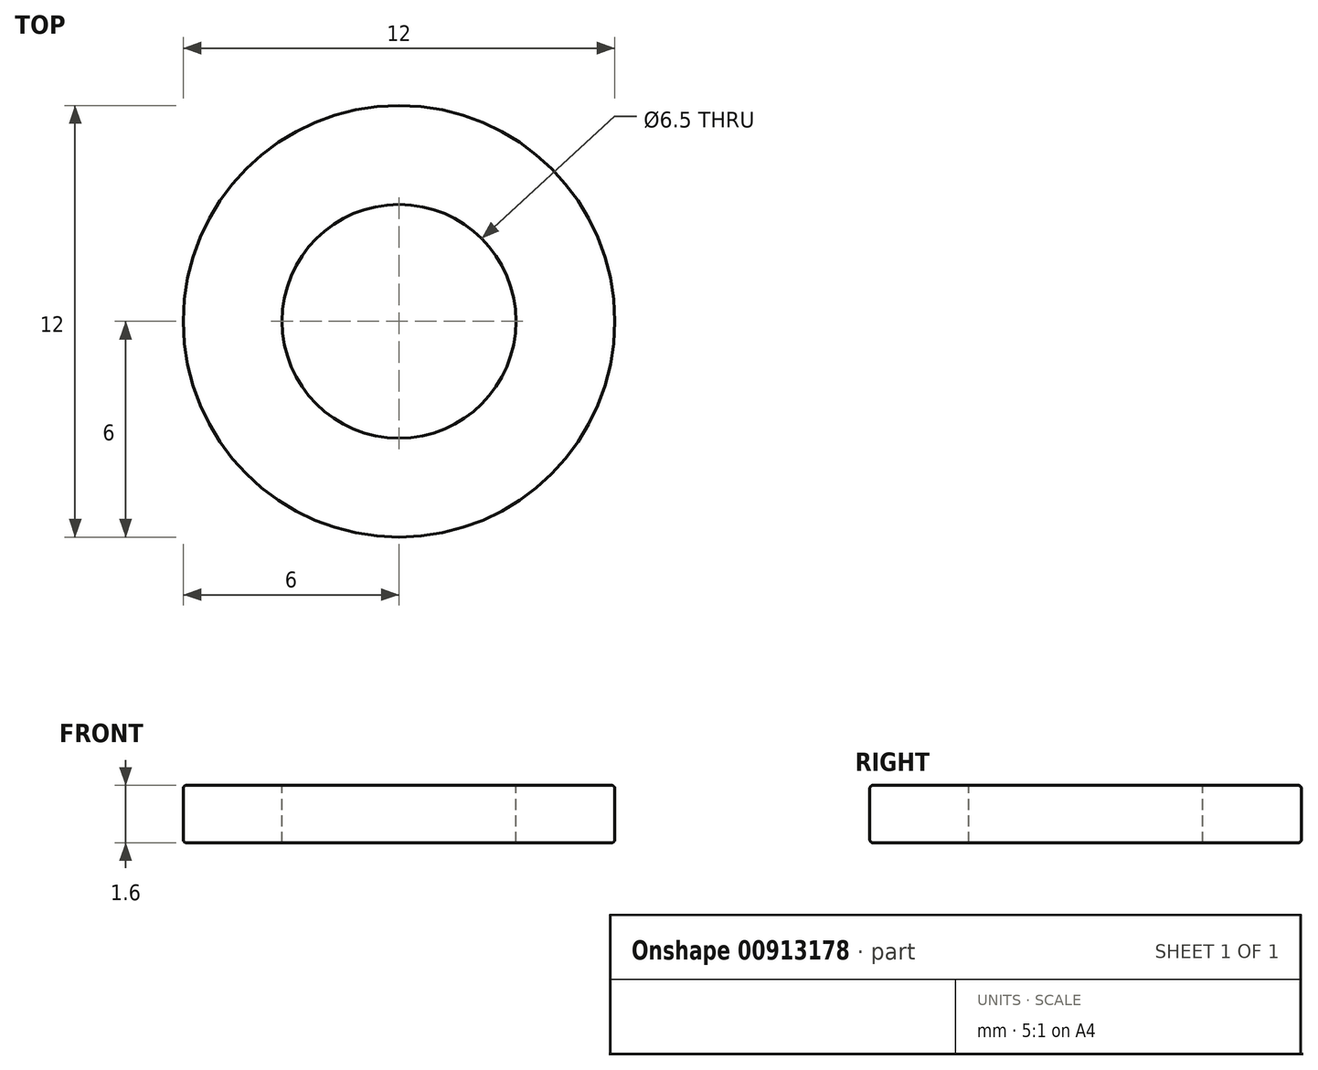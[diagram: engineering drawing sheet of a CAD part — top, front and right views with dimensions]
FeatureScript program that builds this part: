
annotation { "Feature Type Name" : "Feature", "Feature Type Description" : "" }
export const myFeature = defineFeature(function(context is Context, id is Id, definition is map)
    precondition{}
    {
        {
            var Q0;
            Q0=qCreatedBy(makeId("Top.planeOp"),FACE);
            var sketch = newSketch(context, id + "F0", { "sketchPlane" : qUnion([Q0])});
            skCircle(sketch, "E0", {"center": v(0, 0) * mm, "radius": 3.25 * mm});
            skCircle(sketch, "E1", {"center": v(0, 0) * mm, "radius": 6 * mm});
            skSolve(sketch);
        }
        {
            var Q0;
            Q0=makeQuery(id+"F0.imprint","IMPRINT",FACE,{"disambiguationData":[TD([[makeQuery(id+"F0.imprint","IMPRINT",EDGE,{"derivedFrom":sQuery(id+"F0.wireOp",EDGE,"E0")}),-1.0]])]});
            extrude(context, id + "F1", {"entities" : qUnion([Q0]), "oppositeDirection" : true, "depth" : 1.6 * mm, "offsetDistance" : 25 * mm});
        }
        {
            var Q0;
            Q0=makeQuery(id+"F1.opExtrude","CAP_EDGE",EDGE,{"disambiguationData":[OSD([sQuery(id+"F0.wireOp",EDGE,"E1")])],"isStart":true});
            var Q1;
            Q1=makeQuery(id+"F1.opExtrude","CAP_EDGE",EDGE,{"disambiguationData":[OSD([sQuery(id+"F0.wireOp",EDGE,"E1")])],"isStart":false});
            fillet(context, id + "F2", {"entities" : qUnion([Q0, Q1]), "radius" : .1 * mm, "tangentPropagation" : true, "allowEdgeOverflow" : false});
        }
    });
